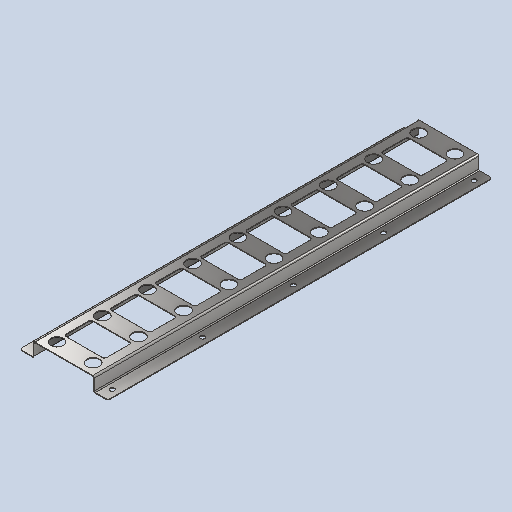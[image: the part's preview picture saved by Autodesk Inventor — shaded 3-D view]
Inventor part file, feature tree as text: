
AUTODESK INVENTOR PART (.ipt)
format: ipt  version: 2022 (Build 260153000, 153)  size: 393,728 bytes
history: native  units: mm
features: other x5, sketch x4, sheet_metal_op x3, pattern_linear x3, fillet x2
ambient origin geometry x8: Origin, YZ Plane, XZ Plane, XY Plane, X Axis, Y Axis, Z Axis, Center Point
bodies: Solid1 (feature_tree)
feature tree (17):
  sheet_metal_op  "Contour Flange1"
  fillet  "Fillet1"  Radius=30.0mm
  pattern_linear  "Rectangular Pattern1"  Count1=3  [1 undecoded]
  pattern_linear  "Rectangular Pattern2"  Spacing1=3.0mm  [1 undecoded]
  fillet  "Fillet2"  Radius=1.5mm
  pattern_linear  "Rectangular Pattern3"  Count1=85  [1 undecoded]
  sketch  "Sketch1"  dims[d2=135.0mm]
  other  "Plate1"
  sheet_metal_op  "Bend1"
  sheet_metal_op  "Corner1"
  sketch  "Sketch2"  dims[d3=1.5mm]
  sketch  "Sketch3"  dims[d4=1.5mm]
  sketch  "Sketch5"  dims[d5=0.75mm d6=3.0mm d7=1.5mm d8=850.0mm d9=2.0mm d10=0.5mm d11=6.0mm d12=1.5mm d13=1.5mm d14=5.0mm d15=80.0mm d16=28.0mm d17=1.5mm d18=0.0mm d19=90.0mm d21=100.0mm d22=10.0mm d23=165.0mm d24=1.5mm d25=0.0mm d26=50.0mm d28=200.0mm d42=5.0mm d43=20.0mm d44=20.0mm d45=5.0mm d46=1.5mm d47=0.0mm d48=5.0mm d49=80.0mm d51=100.0mm]
  other  "Cut1"
  other  "Cut2"
  other  "Cut4"
  other  "Definition1"
note: 3 required parameter values undecoded (feature->parameter linkage not recoverable at this tier; creation-order binding heuristic only, values carry confidence <= 0.55)
